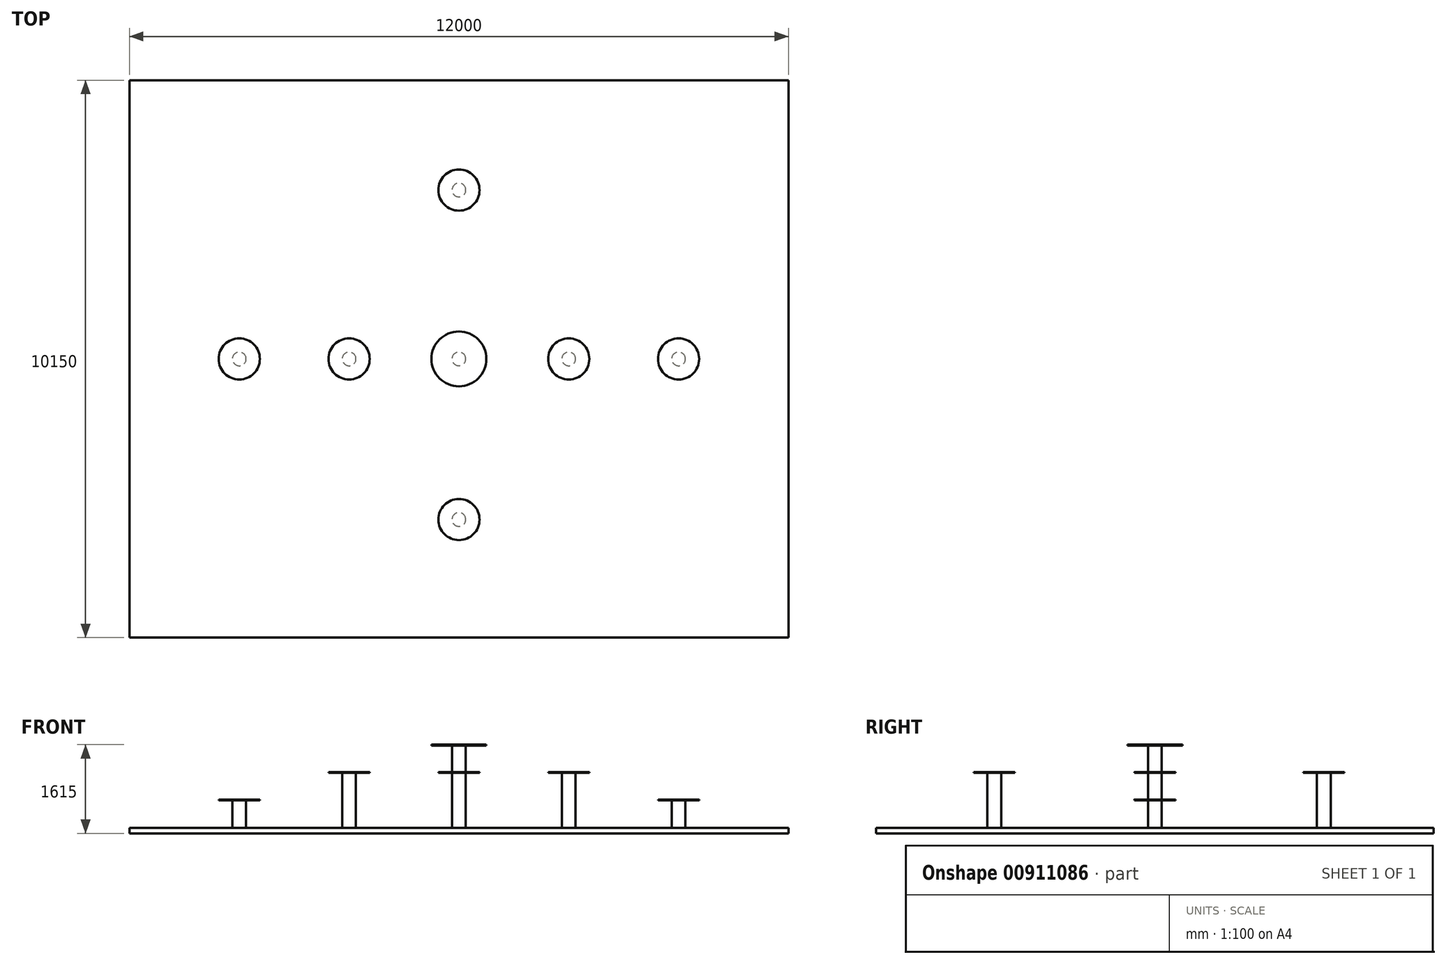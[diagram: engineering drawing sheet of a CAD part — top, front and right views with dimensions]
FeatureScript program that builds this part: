
annotation { "Feature Type Name" : "Feature", "Feature Type Description" : "" }
export const myFeature = defineFeature(function(context is Context, id is Id, definition is map)
    precondition{}
    {
        {
            var Q0;
            Q0=qCreatedBy(makeId("Front.planeOp"),FACE);
            var sketch = newSketch(context, id + "F0", { "sketchPlane" : qUnion([Q0])});
            skLineSegment(sketch, "E0.bottom", {"start": v(-613.58, 0) * mm, "end": v(11386.42, 0) * mm});
            skLineSegment(sketch, "E0.top", {"start": v(-613.58, 100) * mm, "end": v(11386.42, 100) * mm});
            skLineSegment(sketch, "E0.left", {"start": v(-613.58, 0) * mm, "end": v(-613.58, 100) * mm});
            skLineSegment(sketch, "E0.right", {"start": v(11386.42, 0) * mm, "end": v(11386.42, 100) * mm});
            skSolve(sketch);
        }
        {
            var Q0;
            Q0=makeQuery(id+"F0.imprint","IMPRINT",FACE,{"disambiguationData":[TD([[makeQuery(id+"F0.imprint","IMPRINT",EDGE,{"derivedFrom":sQuery(id+"F0.wireOp",EDGE,"E0.bottom")}),1.0]])]});
            extrude(context, id + "F1", {"entities" : qUnion([Q0]), "depth" : 10150 * mm, "offsetDistance" : 25 * mm});
        }
        {
            var Q0;
            Q0=makeQuery(id+"F1.opExtrude","SWEPT_FACE",FACE,{"disambiguationData":[OSD([sQuery(id+"F0.wireOp",EDGE,"E0.top")])]});
            var sketch = newSketch(context, id + "F2", { "sketchPlane" : qUnion([Q0])});
            skLineSegment(sketch, "E1", {"start": v(5386.42, -10150) * mm, "end": v(5386.42, 0) * mm});
            skLineSegment(sketch, "E2", {"start": v(-613.58, -5075) * mm, "end": v(11386.42, -5075) * mm});
            skLineSegment(sketch, "E3.0", {"start": v(7386.42, -10150) * mm, "end": v(7386.42, 0) * mm});
            skSolve(sketch);
        }
        {
            var Q0;
            {var subQ0=sQuery(id+"F2.wireOp",EDGE,"E1");var subQ1=sQuery(id+"F0.wireOp",EDGE,"E0.top");var subQ2=makeQuery(id+"F1.opExtrude","CAP_EDGE",EDGE,{"disambiguationData":[OSD([subQ1])],"isStart":true});var subQ3=makeQuery(id+"F2.imprint","INTERSECT",VERTEX,{"derivedFrom":[subQ2,subQ0]});Q0=makeQuery(id+"F2.imprint","IMPRINT",FACE,{"disambiguationData":[TD([[makeQuery(id+"F2.imprint","IMPRINT",EDGE,{"disambiguationData":[TD([[subQ3,1.0]])],"derivedFrom":subQ0}),1.0]])]});}
            var sketch = newSketch(context, id + "F3", { "sketchPlane" : qUnion([Q0])});
            skCircle(sketch, "E4", {"center": v(5386.49, -5074.55) * mm, "radius": 125 * mm});
            skSolve(sketch);
        }
        {
            var Q0;
            {var subQ1=sQuery(id+"F0.wireOp",EDGE,"E0.top");var subQ4=sQuery(id+"F2.wireOp",EDGE,"E3.0");var subQ6=makeQuery(id+"F1.opExtrude","CAP_EDGE",EDGE,{"disambiguationData":[OSD([subQ1])],"isStart":true});var subQ8=makeQuery(id+"F2.imprint","INTERSECT",VERTEX,{"derivedFrom":[subQ6,subQ4]});Q0=makeQuery(id+"F2.imprint","IMPRINT",FACE,{"disambiguationData":[TD([[makeQuery(id+"F2.imprint","IMPRINT",EDGE,{"disambiguationData":[TD([[subQ8,1.0]])],"derivedFrom":subQ4}),-1.0]])]});}
            var sketch = newSketch(context, id + "F4", { "sketchPlane" : qUnion([Q0])});
            skLineSegment(sketch, "E5.0", {"start": v(9386.42, -10150) * mm, "end": v(9386.42, 0) * mm});
            skSolve(sketch);
        }
        {
            var Q0;
            {var subQ0=sQuery(id+"F2.wireOp",EDGE,"E1");var subQ1=sQuery(id+"F0.wireOp",EDGE,"E0.top");var subQ2=makeQuery(id+"F1.opExtrude","CAP_EDGE",EDGE,{"disambiguationData":[OSD([subQ1])],"isStart":true});var subQ3=makeQuery(id+"F2.imprint","INTERSECT",VERTEX,{"derivedFrom":[subQ2,subQ0]});Q0=makeQuery(id+"F2.imprint","IMPRINT",FACE,{"disambiguationData":[TD([[makeQuery(id+"F2.imprint","IMPRINT",EDGE,{"disambiguationData":[TD([[subQ3,1.0]])],"derivedFrom":subQ0}),1.0]])]});}
            var sketch = newSketch(context, id + "F5", { "sketchPlane" : qUnion([Q0])});
            skLineSegment(sketch, "E6.0", {"start": v(3386.42, -10150) * mm, "end": v(3386.42, 0) * mm});
            skLineSegment(sketch, "E7.0", {"start": v(1386.42, -10150) * mm, "end": v(1386.42, 0) * mm});
            skSolve(sketch);
        }
        {
            var Q0;
            {var subQ0=sQuery(id+"F2.wireOp",EDGE,"E1");var subQ1=makeQuery(id+"F1.opExtrude","CAP_EDGE",EDGE,{"disambiguationData":[OSD([sQuery(id+"F0.wireOp",EDGE,"E0.top")])],"isStart":true});var subQ2=makeQuery(id+"F2.imprint","INTERSECT",VERTEX,{"derivedFrom":[subQ1,subQ0]});Q0=makeQuery(id+"F2.imprint","IMPRINT",FACE,{"disambiguationData":[TD([[makeQuery(id+"F2.imprint","IMPRINT",EDGE,{"disambiguationData":[TD([[subQ2,1.0]])],"derivedFrom":subQ0}),-1.0]])]});}
            var sketch = newSketch(context, id + "F6", { "sketchPlane" : qUnion([Q0])});
            skCircle(sketch, "E8", {"center": v(7386.36, -5074.91) * mm, "radius": 125 * mm});
            skSolve(sketch);
        }
        {
            var Q0;
            {var subQ1=sQuery(id+"F0.wireOp",EDGE,"E0.top");var subQ2=makeQuery(id+"F1.opExtrude","CAP_EDGE",EDGE,{"disambiguationData":[OSD([subQ1])],"isStart":true});var subQ4=sQuery(id+"F2.wireOp",EDGE,"E3.0");var subQ5=makeQuery(id+"F2.imprint","INTERSECT",VERTEX,{"derivedFrom":[subQ2,subQ4]});var subQ12=makeQuery(id+"F2.imprint","IMPRINT",EDGE,{"disambiguationData":[TD([[subQ5,1.0]])],"derivedFrom":subQ4});Q0=makeQuery(id+"F4.imprint","IMPRINT",FACE,{"disambiguationData":[TD([[makeQuery(id+"F4.imprint","IMPRINT",EDGE,{"derivedFrom":subQ12}),-1.0]])]});}
            var sketch = newSketch(context, id + "F7", { "sketchPlane" : qUnion([Q0])});
            skCircle(sketch, "E9", {"center": v(9386.38, -5074.79) * mm, "radius": 125 * mm});
            skSolve(sketch);
        }
        {
            var Q0;
            {var subQ0=sQuery(id+"F2.wireOp",EDGE,"E1");var subQ1=sQuery(id+"F0.wireOp",EDGE,"E0.top");var subQ2=makeQuery(id+"F1.opExtrude","CAP_EDGE",EDGE,{"disambiguationData":[OSD([subQ1])],"isStart":true});var subQ3=makeQuery(id+"F2.imprint","INTERSECT",VERTEX,{"derivedFrom":[subQ2,subQ0]});Q0=makeQuery(id+"F2.imprint","IMPRINT",FACE,{"disambiguationData":[TD([[makeQuery(id+"F2.imprint","IMPRINT",EDGE,{"disambiguationData":[TD([[subQ3,1.0]])],"derivedFrom":subQ0}),1.0]])]});}
            var sketch = newSketch(context, id + "F8", { "sketchPlane" : qUnion([Q0])});
            skCircle(sketch, "E10", {"center": v(3386.4, -5075.13) * mm, "radius": 125 * mm});
            skSolve(sketch);
        }
        {
            var Q0;
            {var subQ1=sQuery(id+"F0.wireOp",EDGE,"E0.top");var subQ2=makeQuery(id+"F1.opExtrude","CAP_EDGE",EDGE,{"disambiguationData":[OSD([subQ1])],"isStart":true});var subQ3=makeQuery(id+"F1.opExtrude","SWEPT_EDGE",EDGE,{"disambiguationData":[OSD([subQ1,sQuery(id+"F0.wireOp",EDGE,"E0.left")])]});var subQ4=makeQuery(id+"F2.imprint","INTERSECT",VERTEX,{"derivedFrom":[subQ3,subQ2]});var subQ12=makeQuery(id+"F2.imprint","IMPRINT",EDGE,{"disambiguationData":[TD([[subQ4,1.0]])],"derivedFrom":subQ3});Q0=makeQuery(id+"F5.imprint","IMPRINT",FACE,{"disambiguationData":[TD([[makeQuery(id+"F5.imprint","IMPRINT",EDGE,{"derivedFrom":subQ12}),-1.0]])]});}
            var sketch = newSketch(context, id + "F9", { "sketchPlane" : qUnion([Q0])});
            skCircle(sketch, "E11", {"center": v(1386.4, -5075.1) * mm, "radius": 125 * mm});
            skSolve(sketch);
        }
        {
            var Q0;
            {var subQ0=sQuery(id+"F3.wireOp",EDGE,"E4");var subQ1=sQuery(id+"F2.wireOp",EDGE,"E1");var subQ2=sQuery(id+"F0.wireOp",EDGE,"E0.top");var subQ5=makeQuery(id+"F2.imprint","IMPRINT",EDGE,{"disambiguationData":[TD([[makeQuery(id+"F2.imprint","INTERSECT",VERTEX,{"derivedFrom":[makeQuery(id+"F1.opExtrude","CAP_EDGE",EDGE,{"disambiguationData":[OSD([subQ2])],"isStart":true}),subQ1]}),1.0]])],"derivedFrom":subQ1});var subQ6=makeQuery(id+"F3.imprint","INTERSECT",VERTEX,{"derivedFrom":[subQ5,subQ0]});Q0=makeQuery(id+"F3.imprint","IMPRINT",FACE,{"disambiguationData":[TD([[makeQuery(id+"F3.imprint","IMPRINT",EDGE,{"disambiguationData":[TD([[subQ6,-1.0]])],"derivedFrom":subQ0}),1.0]])]});}
            var Q1;
            {var subQ0=sQuery(id+"F3.wireOp",EDGE,"E4");var subQ1=sQuery(id+"F2.wireOp",EDGE,"E1");var subQ2=sQuery(id+"F0.wireOp",EDGE,"E0.top");var subQ5=makeQuery(id+"F2.imprint","IMPRINT",EDGE,{"disambiguationData":[TD([[makeQuery(id+"F2.imprint","INTERSECT",VERTEX,{"derivedFrom":[makeQuery(id+"F1.opExtrude","CAP_EDGE",EDGE,{"disambiguationData":[OSD([subQ2])],"isStart":true}),subQ1]}),1.0]])],"derivedFrom":subQ1});var subQ6=makeQuery(id+"F3.imprint","INTERSECT",VERTEX,{"derivedFrom":[subQ5,subQ0]});Q1=makeQuery(id+"F3.imprint","IMPRINT",FACE,{"disambiguationData":[TD([[makeQuery(id+"F3.imprint","IMPRINT",EDGE,{"disambiguationData":[TD([[subQ6,1.0]])],"derivedFrom":subQ0}),1.0]])]});}
            extrude(context, id + "F10", {"entities" : qUnion([Q0, Q1]), "operationType" : NewBodyOperationType.ADD, "depth" : 1500 * mm, "offsetDistance" : 25 * mm});
        }
        {
            var Q0;
            {var subQ0=sQuery(id+"F9.wireOp",EDGE,"E11");var subQ1=sQuery(id+"F5.wireOp",EDGE,"E7.0");var subQ2=sQuery(id+"F0.wireOp",EDGE,"E0.top");var subQ3=makeQuery(id+"F1.opExtrude","CAP_EDGE",EDGE,{"disambiguationData":[OSD([subQ2])],"isStart":true});var subQ6=sQuery(id+"F2.wireOp",EDGE,"E1");var subQ11=makeQuery(id+"F5.imprint","IMPRINT",EDGE,{"disambiguationData":[TD([[makeQuery(id+"F5.imprint","INTERSECT",VERTEX,{"derivedFrom":[makeQuery(id+"F2.imprint","IMPRINT",EDGE,{"disambiguationData":[TD([[makeQuery(id+"F2.imprint","INTERSECT",VERTEX,{"derivedFrom":[subQ3,subQ6]}),1.0]])],"derivedFrom":subQ3}),subQ1]}),1.0]])],"derivedFrom":subQ1});var subQ12=makeQuery(id+"F9.imprint","INTERSECT",VERTEX,{"derivedFrom":[subQ11,subQ0]});Q0=makeQuery(id+"F9.imprint","IMPRINT",FACE,{"disambiguationData":[TD([[makeQuery(id+"F9.imprint","IMPRINT",EDGE,{"disambiguationData":[TD([[subQ12,-1.0]])],"derivedFrom":subQ0}),1.0]])]});}
            var Q1;
            {var subQ0=sQuery(id+"F9.wireOp",EDGE,"E11");var subQ1=sQuery(id+"F5.wireOp",EDGE,"E7.0");var subQ2=sQuery(id+"F0.wireOp",EDGE,"E0.top");var subQ3=makeQuery(id+"F1.opExtrude","CAP_EDGE",EDGE,{"disambiguationData":[OSD([subQ2])],"isStart":true});var subQ6=sQuery(id+"F2.wireOp",EDGE,"E1");var subQ11=makeQuery(id+"F5.imprint","IMPRINT",EDGE,{"disambiguationData":[TD([[makeQuery(id+"F5.imprint","INTERSECT",VERTEX,{"derivedFrom":[makeQuery(id+"F2.imprint","IMPRINT",EDGE,{"disambiguationData":[TD([[makeQuery(id+"F2.imprint","INTERSECT",VERTEX,{"derivedFrom":[subQ3,subQ6]}),1.0]])],"derivedFrom":subQ3}),subQ1]}),1.0]])],"derivedFrom":subQ1});var subQ12=makeQuery(id+"F9.imprint","INTERSECT",VERTEX,{"derivedFrom":[subQ11,subQ0]});Q1=makeQuery(id+"F9.imprint","IMPRINT",FACE,{"disambiguationData":[TD([[makeQuery(id+"F9.imprint","IMPRINT",EDGE,{"disambiguationData":[TD([[subQ12,1.0]])],"derivedFrom":subQ0}),1.0]])]});}
            var Q2;
            {var subQ0=sQuery(id+"F7.wireOp",EDGE,"E9");var subQ1=sQuery(id+"F4.wireOp",EDGE,"E5.0");var subQ2=sQuery(id+"F0.wireOp",EDGE,"E0.top");var subQ3=makeQuery(id+"F1.opExtrude","CAP_EDGE",EDGE,{"disambiguationData":[OSD([subQ2])],"isStart":true});var subQ5=sQuery(id+"F2.wireOp",EDGE,"E3.0");var subQ6=makeQuery(id+"F2.imprint","INTERSECT",VERTEX,{"derivedFrom":[subQ3,subQ5]});var subQ11=makeQuery(id+"F4.imprint","IMPRINT",EDGE,{"disambiguationData":[TD([[makeQuery(id+"F4.imprint","INTERSECT",VERTEX,{"derivedFrom":[makeQuery(id+"F2.imprint","IMPRINT",EDGE,{"disambiguationData":[TD([[subQ6,-1.0]])],"derivedFrom":subQ3}),subQ1]}),1.0]])],"derivedFrom":subQ1});var subQ12=makeQuery(id+"F7.imprint","INTERSECT",VERTEX,{"derivedFrom":[subQ11,subQ0]});Q2=makeQuery(id+"F7.imprint","IMPRINT",FACE,{"disambiguationData":[TD([[makeQuery(id+"F7.imprint","IMPRINT",EDGE,{"disambiguationData":[TD([[subQ12,1.0]])],"derivedFrom":subQ0}),1.0]])]});}
            var Q3;
            {var subQ0=sQuery(id+"F7.wireOp",EDGE,"E9");var subQ1=sQuery(id+"F4.wireOp",EDGE,"E5.0");var subQ2=sQuery(id+"F0.wireOp",EDGE,"E0.top");var subQ3=makeQuery(id+"F1.opExtrude","CAP_EDGE",EDGE,{"disambiguationData":[OSD([subQ2])],"isStart":true});var subQ5=sQuery(id+"F2.wireOp",EDGE,"E3.0");var subQ6=makeQuery(id+"F2.imprint","INTERSECT",VERTEX,{"derivedFrom":[subQ3,subQ5]});var subQ11=makeQuery(id+"F4.imprint","IMPRINT",EDGE,{"disambiguationData":[TD([[makeQuery(id+"F4.imprint","INTERSECT",VERTEX,{"derivedFrom":[makeQuery(id+"F2.imprint","IMPRINT",EDGE,{"disambiguationData":[TD([[subQ6,-1.0]])],"derivedFrom":subQ3}),subQ1]}),1.0]])],"derivedFrom":subQ1});var subQ12=makeQuery(id+"F7.imprint","INTERSECT",VERTEX,{"derivedFrom":[subQ11,subQ0]});Q3=makeQuery(id+"F7.imprint","IMPRINT",FACE,{"disambiguationData":[TD([[makeQuery(id+"F7.imprint","IMPRINT",EDGE,{"disambiguationData":[TD([[subQ12,-1.0]])],"derivedFrom":subQ0}),1.0]])]});}
            var Q4;
            Q4=sQuery(id+"F9.wireOp",EDGE,"E11");
            var Q5;
            Q5=sQuery(id+"F7.wireOp",EDGE,"E9");
            extrude(context, id + "F11", {"entities" : qUnion([Q0, Q1, Q2, Q3]), "surfaceOperationType" : NewSurfaceOperationType.ADD, "surfaceEntities" : qUnion([Q4, Q5]), "depth" : 500 * mm, "offsetDistance" : 25 * mm});
        }
        {
            var Q0;
            {var subQ0=sQuery(id+"F8.wireOp",EDGE,"E10");var subQ1=sQuery(id+"F2.wireOp",EDGE,"E2");var subQ2=makeQuery(id+"F2.imprint","IMPRINT",EDGE,{"disambiguationData":[TD([[makeQuery(id+"F2.imprint","INTERSECT",VERTEX,{"derivedFrom":[sQuery(id+"F2.wireOp",EDGE,"E1"),subQ1]}),1.0]])],"derivedFrom":subQ1});var subQ3=makeQuery(id+"F8.imprint","INTERSECT",VERTEX,{"disambiguationData":[OD(0.0)],"derivedFrom":[subQ2,subQ0]});Q0=makeQuery(id+"F8.imprint","IMPRINT",FACE,{"disambiguationData":[TD([[makeQuery(id+"F8.imprint","IMPRINT",EDGE,{"disambiguationData":[TD([[subQ3,1.0]])],"derivedFrom":subQ0}),1.0]])]});}
            var Q1;
            {var subQ0=sQuery(id+"F8.wireOp",EDGE,"E10");var subQ1=sQuery(id+"F2.wireOp",EDGE,"E2");var subQ2=makeQuery(id+"F2.imprint","IMPRINT",EDGE,{"disambiguationData":[TD([[makeQuery(id+"F2.imprint","INTERSECT",VERTEX,{"derivedFrom":[sQuery(id+"F2.wireOp",EDGE,"E1"),subQ1]}),1.0]])],"derivedFrom":subQ1});var subQ3=makeQuery(id+"F8.imprint","INTERSECT",VERTEX,{"disambiguationData":[OD(0.0)],"derivedFrom":[subQ2,subQ0]});Q1=makeQuery(id+"F8.imprint","IMPRINT",FACE,{"disambiguationData":[TD([[makeQuery(id+"F8.imprint","IMPRINT",EDGE,{"disambiguationData":[TD([[subQ3,-1.0]])],"derivedFrom":subQ0}),1.0]])]});}
            var Q2;
            {var subQ0=sQuery(id+"F6.wireOp",EDGE,"E8");var subQ1=sQuery(id+"F2.wireOp",EDGE,"E2");var subQ4=makeQuery(id+"F2.imprint","IMPRINT",EDGE,{"disambiguationData":[TD([[makeQuery(id+"F2.imprint","INTERSECT",VERTEX,{"derivedFrom":[sQuery(id+"F2.wireOp",EDGE,"E1"),subQ1]}),-1.0]])],"derivedFrom":subQ1});var subQ5=makeQuery(id+"F6.imprint","INTERSECT",VERTEX,{"derivedFrom":[subQ4,subQ0]});Q2=makeQuery(id+"F6.imprint","IMPRINT",FACE,{"disambiguationData":[TD([[makeQuery(id+"F6.imprint","IMPRINT",EDGE,{"disambiguationData":[TD([[subQ5,-1.0]])],"derivedFrom":subQ0}),1.0]])]});}
            var Q3;
            {var subQ0=sQuery(id+"F6.wireOp",EDGE,"E8");var subQ1=sQuery(id+"F2.wireOp",EDGE,"E2");var subQ4=makeQuery(id+"F2.imprint","IMPRINT",EDGE,{"disambiguationData":[TD([[makeQuery(id+"F2.imprint","INTERSECT",VERTEX,{"derivedFrom":[sQuery(id+"F2.wireOp",EDGE,"E1"),subQ1]}),-1.0]])],"derivedFrom":subQ1});var subQ5=makeQuery(id+"F6.imprint","INTERSECT",VERTEX,{"derivedFrom":[subQ4,subQ0]});Q3=makeQuery(id+"F6.imprint","IMPRINT",FACE,{"disambiguationData":[TD([[makeQuery(id+"F6.imprint","IMPRINT",EDGE,{"disambiguationData":[TD([[subQ5,1.0]])],"derivedFrom":subQ0}),1.0]])]});}
            var Q4;
            Q4=sQuery(id+"F8.wireOp",EDGE,"E10");
            var Q5;
            Q5=sQuery(id+"F6.wireOp",EDGE,"E8");
            extrude(context, id + "F12", {"entities" : qUnion([Q0, Q1, Q2, Q3]), "surfaceEntities" : qUnion([Q4, Q5]), "depth" : 1000 * mm, "offsetDistance" : 25 * mm});
        }
        {
            var Q0;
            {var subQ0=sQuery(id+"F0.wireOp",EDGE,"E0.top");var subQ1=makeQuery(id+"F1.opExtrude","CAP_EDGE",EDGE,{"disambiguationData":[OSD([subQ0])],"isStart":true});var subQ4=sQuery(id+"F2.wireOp",EDGE,"E1");var subQ5=makeQuery(id+"F2.imprint","INTERSECT",VERTEX,{"derivedFrom":[subQ1,subQ4]});var subQ6=makeQuery(id+"F2.imprint","IMPRINT",EDGE,{"disambiguationData":[TD([[subQ5,1.0]])],"derivedFrom":subQ1});Q0=makeQuery(id+"F3.imprint","IMPRINT",FACE,{"disambiguationData":[TD([[makeQuery(id+"F3.imprint","IMPRINT",EDGE,{"derivedFrom":subQ6}),-1.0]])]});}
            var sketch = newSketch(context, id + "F13", { "sketchPlane" : qUnion([Q0])});
            skLineSegment(sketch, "E12.0", {"start": v(-613.58, -2000) * mm, "end": v(11386.42, -2000) * mm});
            skSolve(sketch);
        }
        {
            var Q0;
            {var subQ0=sQuery(id+"F0.wireOp",EDGE,"E0.top");var subQ1=makeQuery(id+"F1.opExtrude","CAP_EDGE",EDGE,{"disambiguationData":[OSD([subQ0])],"isStart":true});var subQ4=sQuery(id+"F2.wireOp",EDGE,"E1");var subQ5=makeQuery(id+"F2.imprint","INTERSECT",VERTEX,{"derivedFrom":[subQ1,subQ4]});var subQ6=makeQuery(id+"F2.imprint","IMPRINT",EDGE,{"disambiguationData":[TD([[subQ5,1.0]])],"derivedFrom":subQ1});Q0=makeQuery(id+"F3.imprint","IMPRINT",FACE,{"disambiguationData":[TD([[makeQuery(id+"F3.imprint","IMPRINT",EDGE,{"derivedFrom":subQ6}),-1.0]])]});}
            var sketch = newSketch(context, id + "F14", { "sketchPlane" : qUnion([Q0])});
            skCircle(sketch, "E13", {"center": v(5386.72, -1999.69) * mm, "radius": 125 * mm});
            skSolve(sketch);
        }
        {
            var Q0;
            {var subQ0=sQuery(id+"F2.wireOp",EDGE,"E1");var subQ1=makeQuery(id+"F1.opExtrude","CAP_EDGE",EDGE,{"disambiguationData":[OSD([sQuery(id+"F0.wireOp",EDGE,"E0.top")])],"isStart":false});var subQ2=makeQuery(id+"F2.imprint","INTERSECT",VERTEX,{"derivedFrom":[subQ1,subQ0]});Q0=makeQuery(id+"F2.imprint","IMPRINT",FACE,{"disambiguationData":[TD([[makeQuery(id+"F2.imprint","IMPRINT",EDGE,{"disambiguationData":[TD([[subQ2,-1.0]])],"derivedFrom":subQ0}),-1.0]])]});}
            var sketch = newSketch(context, id + "F15", { "sketchPlane" : qUnion([Q0])});
            skCircle(sketch, "E14", {"center": v(5386.47, -7999.68) * mm, "radius": 125 * mm});
            skSolve(sketch);
        }
        {
            var Q0;
            {var subQ0=sQuery(id+"F14.wireOp",EDGE,"E13");var subQ1=sQuery(id+"F0.wireOp",EDGE,"E0.top");var subQ2=makeQuery(id+"F1.opExtrude","CAP_EDGE",EDGE,{"disambiguationData":[OSD([subQ1])],"isStart":true});var subQ3=sQuery(id+"F2.wireOp",EDGE,"E1");var subQ4=makeQuery(id+"F2.imprint","INTERSECT",VERTEX,{"derivedFrom":[subQ2,subQ3]});var subQ5=makeQuery(id+"F2.imprint","IMPRINT",EDGE,{"disambiguationData":[TD([[subQ4,1.0]])],"derivedFrom":subQ3});var subQ6=makeQuery(id+"F3.imprint","IMPRINT",EDGE,{"disambiguationData":[TD([[makeQuery(id+"F3.imprint","INTERSECT",VERTEX,{"derivedFrom":[subQ5,sQuery(id+"F3.wireOp",EDGE,"E4")]}),-1.0]])],"derivedFrom":subQ5});var subQ7=makeQuery(id+"F14.imprint","INTERSECT",VERTEX,{"disambiguationData":[OD(0.0)],"derivedFrom":[subQ6,subQ0]});Q0=makeQuery(id+"F14.imprint","IMPRINT",FACE,{"disambiguationData":[TD([[makeQuery(id+"F14.imprint","IMPRINT",EDGE,{"disambiguationData":[TD([[subQ7,1.0]])],"derivedFrom":subQ0}),1.0]])]});}
            var Q1;
            {var subQ0=sQuery(id+"F14.wireOp",EDGE,"E13");var subQ1=sQuery(id+"F0.wireOp",EDGE,"E0.top");var subQ2=makeQuery(id+"F1.opExtrude","CAP_EDGE",EDGE,{"disambiguationData":[OSD([subQ1])],"isStart":true});var subQ3=sQuery(id+"F2.wireOp",EDGE,"E1");var subQ4=makeQuery(id+"F2.imprint","INTERSECT",VERTEX,{"derivedFrom":[subQ2,subQ3]});var subQ5=makeQuery(id+"F2.imprint","IMPRINT",EDGE,{"disambiguationData":[TD([[subQ4,1.0]])],"derivedFrom":subQ3});var subQ6=makeQuery(id+"F3.imprint","IMPRINT",EDGE,{"disambiguationData":[TD([[makeQuery(id+"F3.imprint","INTERSECT",VERTEX,{"derivedFrom":[subQ5,sQuery(id+"F3.wireOp",EDGE,"E4")]}),-1.0]])],"derivedFrom":subQ5});var subQ7=makeQuery(id+"F14.imprint","INTERSECT",VERTEX,{"disambiguationData":[OD(0.0)],"derivedFrom":[subQ6,subQ0]});Q1=makeQuery(id+"F14.imprint","IMPRINT",FACE,{"disambiguationData":[TD([[makeQuery(id+"F14.imprint","IMPRINT",EDGE,{"disambiguationData":[TD([[subQ7,-1.0]])],"derivedFrom":subQ0}),1.0]])]});}
            var Q2;
            {var subQ0=sQuery(id+"F15.wireOp",EDGE,"E14");var subQ1=sQuery(id+"F2.wireOp",EDGE,"E1");var subQ2=makeQuery(id+"F2.imprint","IMPRINT",EDGE,{"disambiguationData":[TD([[makeQuery(id+"F2.imprint","INTERSECT",VERTEX,{"derivedFrom":[makeQuery(id+"F1.opExtrude","CAP_EDGE",EDGE,{"disambiguationData":[OSD([sQuery(id+"F0.wireOp",EDGE,"E0.top")])],"isStart":false}),subQ1]}),-1.0]])],"derivedFrom":subQ1});var subQ3=makeQuery(id+"F15.imprint","INTERSECT",VERTEX,{"disambiguationData":[OD(0.0)],"derivedFrom":[subQ2,subQ0]});Q2=makeQuery(id+"F15.imprint","IMPRINT",FACE,{"disambiguationData":[TD([[makeQuery(id+"F15.imprint","IMPRINT",EDGE,{"disambiguationData":[TD([[subQ3,1.0]])],"derivedFrom":subQ0}),1.0]])]});}
            var Q3;
            {var subQ0=sQuery(id+"F15.wireOp",EDGE,"E14");var subQ1=sQuery(id+"F2.wireOp",EDGE,"E1");var subQ2=makeQuery(id+"F2.imprint","IMPRINT",EDGE,{"disambiguationData":[TD([[makeQuery(id+"F2.imprint","INTERSECT",VERTEX,{"derivedFrom":[makeQuery(id+"F1.opExtrude","CAP_EDGE",EDGE,{"disambiguationData":[OSD([sQuery(id+"F0.wireOp",EDGE,"E0.top")])],"isStart":false}),subQ1]}),-1.0]])],"derivedFrom":subQ1});var subQ3=makeQuery(id+"F15.imprint","INTERSECT",VERTEX,{"disambiguationData":[OD(0.0)],"derivedFrom":[subQ2,subQ0]});Q3=makeQuery(id+"F15.imprint","IMPRINT",FACE,{"disambiguationData":[TD([[makeQuery(id+"F15.imprint","IMPRINT",EDGE,{"disambiguationData":[TD([[subQ3,-1.0]])],"derivedFrom":subQ0}),1.0]])]});}
            extrude(context, id + "F16", {"entities" : qUnion([Q0, Q1, Q2, Q3]), "operationType" : NewBodyOperationType.ADD, "depth" : 1000 * mm, "offsetDistance" : 25 * mm});
        }
        {
            var Q0;
            Q0=makeQuery(id+"F16.opExtrude","CAP_FACE",FACE,{"disambiguationData":[OSD([sQuery(id+"F14.wireOp",EDGE,"E13")])],"isStart":false});
            var sketch = newSketch(context, id + "F17", { "sketchPlane" : qUnion([Q0])});
            skCircle(sketch, "E15", {"center": v(5386.72, -1999.69) * mm, "radius": 375 * mm});
            skSolve(sketch);
        }
        {
            var Q0;
            Q0=makeQuery(id+"F17.imprint","IMPRINT",FACE,{"disambiguationData":[TD([[makeQuery(id+"F17.imprint","IMPRINT",EDGE,{"derivedFrom":sQuery(id+"F17.wireOp",EDGE,"E15")}),1.0]])]});
            var Q1;
            Q1=makeQuery(id+"F17.imprint","IMPRINT",FACE,{"disambiguationData":[TD([[makeQuery(id+"F17.imprint","IMPRINT",EDGE,{"derivedFrom":makeQuery(id+"F16.opExtrude","CAP_EDGE",EDGE,{"disambiguationData":[OSD([sQuery(id+"F14.wireOp",EDGE,"E13")])],"isStart":false})}),1.0]])]});
            extrude(context, id + "F18", {"entities" : qUnion([Q0, Q1]), "operationType" : NewBodyOperationType.ADD, "depth" : 15 * mm, "offsetDistance" : 25 * mm});
        }
        {
            var Q0;
            Q0=makeQuery(id+"F10.opExtrude","CAP_FACE",FACE,{"disambiguationData":[OSD([sQuery(id+"F3.wireOp",EDGE,"E4")])],"isStart":false});
            var sketch = newSketch(context, id + "F19", { "sketchPlane" : qUnion([Q0])});
            skCircle(sketch, "E16", {"center": v(5386.49, -5074.55) * mm, "radius": 500 * mm});
            skSolve(sketch);
        }
        {
            var Q0;
            Q0=makeQuery(id+"F19.imprint","IMPRINT",FACE,{"disambiguationData":[TD([[makeQuery(id+"F19.imprint","IMPRINT",EDGE,{"derivedFrom":sQuery(id+"F19.wireOp",EDGE,"E16")}),1.0]])]});
            var Q1;
            Q1=makeQuery(id+"F19.imprint","IMPRINT",FACE,{"disambiguationData":[TD([[makeQuery(id+"F19.imprint","IMPRINT",EDGE,{"derivedFrom":makeQuery(id+"F10.opExtrude","CAP_EDGE",EDGE,{"disambiguationData":[OSD([sQuery(id+"F3.wireOp",EDGE,"E4")])],"isStart":false})}),1.0]])]});
            extrude(context, id + "F20", {"entities" : qUnion([Q0, Q1]), "operationType" : NewBodyOperationType.ADD, "depth" : 15 * mm, "offsetDistance" : 25 * mm});
        }
        {
            var Q0;
            Q0=makeQuery(id+"F16.opExtrude","CAP_FACE",FACE,{"disambiguationData":[OSD([sQuery(id+"F15.wireOp",EDGE,"E14")])],"isStart":false});
            var sketch = newSketch(context, id + "F21", { "sketchPlane" : qUnion([Q0])});
            skCircle(sketch, "E17", {"center": v(5386.47, -7999.68) * mm, "radius": 375 * mm});
            skSolve(sketch);
        }
        {
            var Q0;
            Q0=makeQuery(id+"F21.imprint","IMPRINT",FACE,{"disambiguationData":[TD([[makeQuery(id+"F21.imprint","IMPRINT",EDGE,{"derivedFrom":sQuery(id+"F21.wireOp",EDGE,"E17")}),1.0]])]});
            var Q1;
            Q1=makeQuery(id+"F21.imprint","IMPRINT",FACE,{"disambiguationData":[TD([[makeQuery(id+"F21.imprint","IMPRINT",EDGE,{"derivedFrom":makeQuery(id+"F16.opExtrude","CAP_EDGE",EDGE,{"disambiguationData":[OSD([sQuery(id+"F15.wireOp",EDGE,"E14")])],"isStart":false})}),1.0]])]});
            extrude(context, id + "F22", {"entities" : qUnion([Q0, Q1]), "depth" : 15 * mm, "offsetDistance" : 25 * mm});
        }
        {
            var Q0;
            Q0=makeQuery(id+"F11.opExtrude","CAP_FACE",FACE,{"disambiguationData":[OSD([sQuery(id+"F9.wireOp",EDGE,"E11")])],"isStart":false});
            var sketch = newSketch(context, id + "F23", { "sketchPlane" : qUnion([Q0])});
            skCircle(sketch, "E18", {"center": v(1386.4, -5075.1) * mm, "radius": 375 * mm});
            skSolve(sketch);
        }
        {
            var Q0;
            Q0=makeQuery(id+"F23.imprint","IMPRINT",FACE,{"disambiguationData":[TD([[makeQuery(id+"F23.imprint","IMPRINT",EDGE,{"derivedFrom":sQuery(id+"F23.wireOp",EDGE,"E18")}),1.0]])]});
            var Q1;
            Q1=makeQuery(id+"F23.imprint","IMPRINT",FACE,{"disambiguationData":[TD([[makeQuery(id+"F23.imprint","IMPRINT",EDGE,{"derivedFrom":makeQuery(id+"F11.opExtrude","CAP_EDGE",EDGE,{"disambiguationData":[OSD([sQuery(id+"F9.wireOp",EDGE,"E11")])],"isStart":false})}),1.0]])]});
            extrude(context, id + "F24", {"entities" : qUnion([Q0, Q1]), "operationType" : NewBodyOperationType.ADD, "depth" : 15 * mm, "offsetDistance" : 25 * mm});
        }
        {
            var Q0;
            Q0=makeQuery(id+"F12.opExtrude","CAP_FACE",FACE,{"disambiguationData":[OSD([sQuery(id+"F8.wireOp",EDGE,"E10")])],"isStart":false});
            var sketch = newSketch(context, id + "F25", { "sketchPlane" : qUnion([Q0])});
            skCircle(sketch, "E19", {"center": v(3386.4, -5075.13) * mm, "radius": 375 * mm});
            skSolve(sketch);
        }
        {
            var Q0;
            Q0=makeQuery(id+"F25.imprint","IMPRINT",FACE,{"disambiguationData":[TD([[makeQuery(id+"F25.imprint","IMPRINT",EDGE,{"derivedFrom":sQuery(id+"F25.wireOp",EDGE,"E19")}),1.0]])]});
            var Q1;
            Q1=makeQuery(id+"F25.imprint","IMPRINT",FACE,{"disambiguationData":[TD([[makeQuery(id+"F25.imprint","IMPRINT",EDGE,{"derivedFrom":makeQuery(id+"F12.opExtrude","CAP_EDGE",EDGE,{"disambiguationData":[OSD([sQuery(id+"F8.wireOp",EDGE,"E10")])],"isStart":false})}),1.0]])]});
            extrude(context, id + "F26", {"entities" : qUnion([Q0, Q1]), "operationType" : NewBodyOperationType.ADD, "depth" : 15 * mm, "offsetDistance" : 25 * mm});
        }
        {
            var Q0;
            Q0=makeQuery(id+"F12.opExtrude","CAP_FACE",FACE,{"disambiguationData":[OSD([sQuery(id+"F6.wireOp",EDGE,"E8")])],"isStart":false});
            var sketch = newSketch(context, id + "F27", { "sketchPlane" : qUnion([Q0])});
            skCircle(sketch, "E20", {"center": v(7386.36, -5074.91) * mm, "radius": 375 * mm});
            skSolve(sketch);
        }
        {
            var Q0;
            Q0=makeQuery(id+"F27.imprint","IMPRINT",FACE,{"disambiguationData":[TD([[makeQuery(id+"F27.imprint","IMPRINT",EDGE,{"derivedFrom":sQuery(id+"F27.wireOp",EDGE,"E20")}),1.0]])]});
            var Q1;
            Q1=makeQuery(id+"F27.imprint","IMPRINT",FACE,{"disambiguationData":[TD([[makeQuery(id+"F27.imprint","IMPRINT",EDGE,{"derivedFrom":makeQuery(id+"F12.opExtrude","CAP_EDGE",EDGE,{"disambiguationData":[OSD([sQuery(id+"F6.wireOp",EDGE,"E8")])],"isStart":false})}),1.0]])]});
            extrude(context, id + "F28", {"entities" : qUnion([Q0, Q1]), "operationType" : NewBodyOperationType.ADD, "depth" : 15 * mm, "offsetDistance" : 25 * mm});
        }
        {
            var Q0;
            Q0=makeQuery(id+"F11.opExtrude","CAP_FACE",FACE,{"disambiguationData":[OSD([sQuery(id+"F7.wireOp",EDGE,"E9")])],"isStart":false});
            var sketch = newSketch(context, id + "F29", { "sketchPlane" : qUnion([Q0])});
            skCircle(sketch, "E21", {"center": v(9386.38, -5074.79) * mm, "radius": 375 * mm});
            skSolve(sketch);
        }
        {
            var Q0;
            Q0=makeQuery(id+"F29.imprint","IMPRINT",FACE,{"disambiguationData":[TD([[makeQuery(id+"F29.imprint","IMPRINT",EDGE,{"derivedFrom":sQuery(id+"F29.wireOp",EDGE,"E21")}),1.0]])]});
            var Q1;
            Q1=makeQuery(id+"F29.imprint","IMPRINT",FACE,{"disambiguationData":[TD([[makeQuery(id+"F29.imprint","IMPRINT",EDGE,{"derivedFrom":makeQuery(id+"F11.opExtrude","CAP_EDGE",EDGE,{"disambiguationData":[OSD([sQuery(id+"F7.wireOp",EDGE,"E9")])],"isStart":false})}),1.0]])]});
            extrude(context, id + "F30", {"entities" : qUnion([Q0, Q1]), "operationType" : NewBodyOperationType.ADD, "depth" : 15 * mm, "offsetDistance" : 25 * mm});
        }
    });
